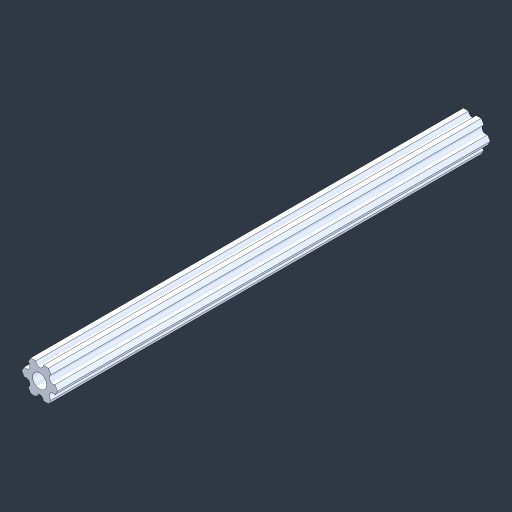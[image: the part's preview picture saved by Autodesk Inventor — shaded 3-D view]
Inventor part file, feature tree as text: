
AUTODESK INVENTOR PART (.ipt)
format: ipt  version: 2024.3 (Build 283343000, 343)  size: 106,496 bytes
history: native  units: mm (DEFAULTED — no unit token found)
features: extrude x1, sketch x1, other x1
ambient origin geometry x8: Origin, YZ Plane, XZ Plane, XY Plane, X Axis, Y Axis, Z Axis, Center Point
bodies: Solid1 (feature_tree)
feature tree (3):
  extrude  "Extrusion1"  [1 undecoded]
  sketch  "Sketch1"  dims[d0=177.8mm d1=0.0mm]
  other  "Boss-Extrude1"
note: 1 required parameter value undecoded (feature->parameter linkage not recoverable at this tier; creation-order binding heuristic only, values carry confidence <= 0.55)
